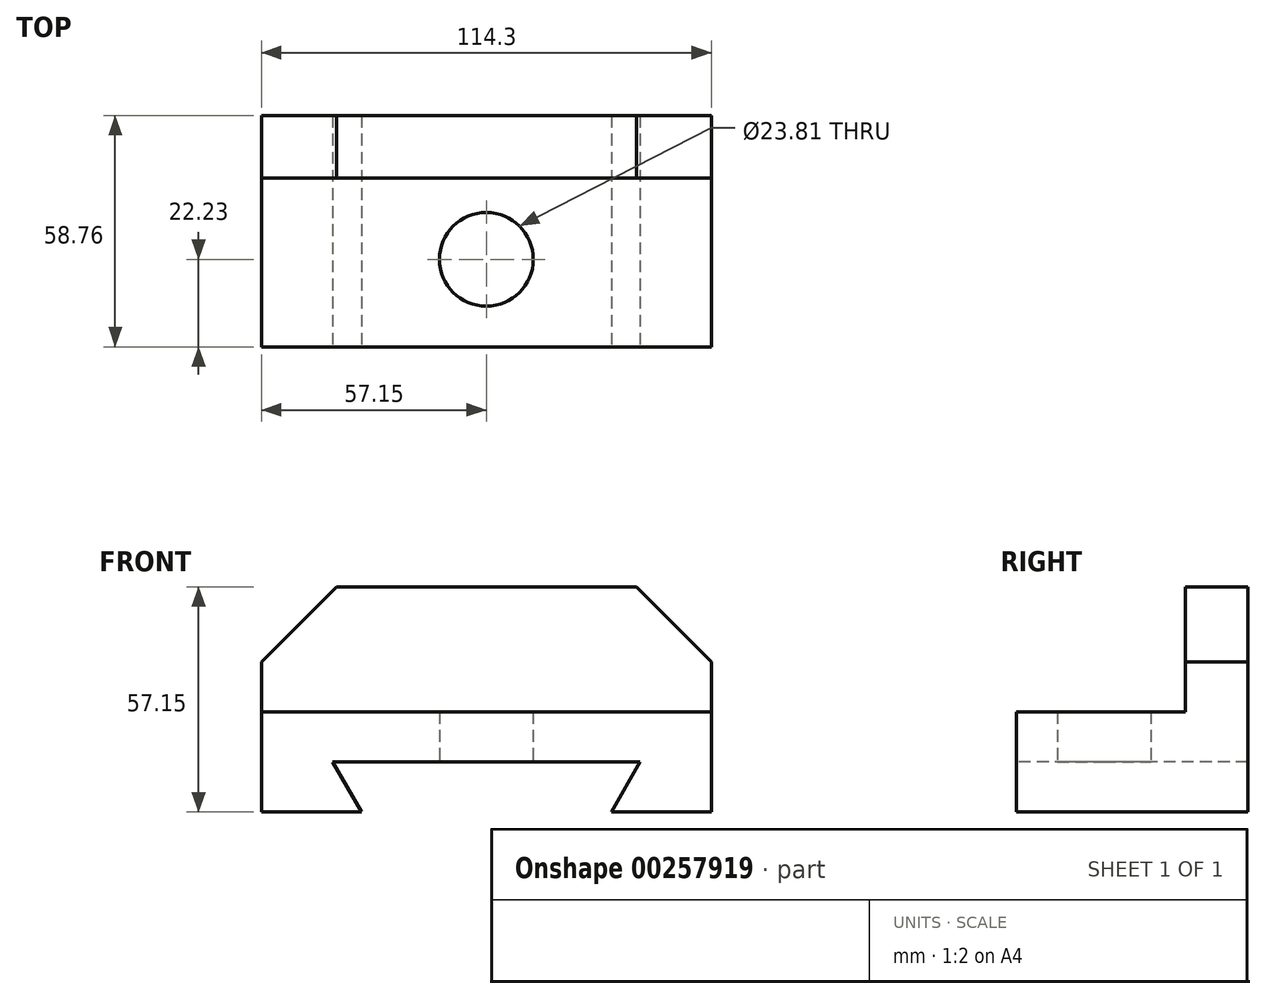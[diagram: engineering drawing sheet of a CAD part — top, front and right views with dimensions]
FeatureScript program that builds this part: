
annotation { "Feature Type Name" : "Feature", "Feature Type Description" : "" }
export const myFeature = defineFeature(function(context is Context, id is Id, definition is map)
    precondition{}
    {
        {
            var Q0;
            Q0=qCreatedBy(makeId("Top.planeOp"),FACE);
            var sketch = newSketch(context, id + "F0", { "sketchPlane" : qUnion([Q0])});
            skCircle(sketch, "E0", {"center": v(0, 0) * mm, "radius": 11.9 * mm});
            skLineSegment(sketch, "E1", {"start": v(0, 0) * mm, "end": v(0, -22.23) * mm});
            skLineSegment(sketch, "E2", {"start": v(0, -22.23) * mm, "end": v(-57.15, -22.23) * mm});
            skLineSegment(sketch, "E3.MirrorCS", {"start": v(0, -22.23) * mm, "end": v(57.15, -22.23) * mm});
            skLineSegment(sketch, "E4", {"start": v(0, 0) * mm, "end": v(-57.15, 0) * mm});
            skLineSegment(sketch, "E5", {"start": v(-57.15, 0) * mm, "end": v(-57.15, -22.23) * mm});
            skPoint(sketch, "E6.MirrorCS.end.orphan", {"position": v(57.15, 22.22) * mm});
            skPoint(sketch, "E6.MirrorCS.start.orphan", {"position": v(57.15, -22.23) * mm});
            skPoint(sketch, "E7.MirrorCS.end.orphan", {"position": v(0, 22.22) * mm});
            skLineSegment(sketch, "E8", {"start": v(-57.15, 0) * mm, "end": v(-57.15, 20.65) * mm});
            skLineSegment(sketch, "E9.MirrorCS", {"start": v(57.15, 0) * mm, "end": v(57.15, 20.65) * mm});
            skLineSegment(sketch, "E10.MirrorCS", {"start": v(0, 0) * mm, "end": v(57.15, 0) * mm});
            skLineSegment(sketch, "E11.MirrorCS", {"start": v(57.15, 0) * mm, "end": v(57.15, -22.23) * mm});
            skLineSegment(sketch, "E12", {"start": v(-57.15, 20.65) * mm, "end": v(57.15, 20.65) * mm});
            skLineSegment(sketch, "E13", {"start": v(-57.15, 20.65) * mm, "end": v(-57.15, 36.53) * mm});
            skLineSegment(sketch, "E14", {"start": v(-57.15, 36.53) * mm, "end": v(57.15, 36.53) * mm});
            skLineSegment(sketch, "E15", {"start": v(57.15, 20.65) * mm, "end": v(57.15, 36.53) * mm});
            skLineSegment(sketch, "E16", {"start": v(-57.15, 36.53) * mm, "end": v(-38.1, 36.53) * mm});
            skLineSegment(sketch, "E17", {"start": v(-38.1, 36.53) * mm, "end": v(-38.1, 20.65) * mm});
            skLineSegment(sketch, "E18.MirrorCS", {"start": v(38.1, 36.53) * mm, "end": v(38.1, 20.65) * mm});
            skLineSegment(sketch, "E19.MirrorCS", {"start": v(57.15, 36.53) * mm, "end": v(38.1, 36.53) * mm});
            skSolve(sketch);
        }
        {
            var Q0;
            {var subQ0=sQuery(id+"F0.wireOp",EDGE,"E13");Q0=makeQuery(id+"F0.imprint","IMPRINT",FACE,{"disambiguationData":[TD([[makeQuery(id+"F0.imprint","IMPRINT",EDGE,{"derivedFrom":subQ0}),-1.0]])]});}
            var Q1;
            Q1=makeQuery(id+"F0.imprint","IMPRINT",FACE,{"disambiguationData":[TD([[makeQuery(id+"F0.imprint","IMPRINT",EDGE,{"derivedFrom":sQuery(id+"F0.wireOp",EDGE,"E14")}),-1.0]])]});
            var Q2;
            {var subQ0=sQuery(id+"F0.wireOp",EDGE,"E15");Q2=makeQuery(id+"F0.imprint","IMPRINT",FACE,{"disambiguationData":[TD([[makeQuery(id+"F0.imprint","IMPRINT",EDGE,{"derivedFrom":subQ0}),1.0]])]});}
            extrude(context, id + "F1", {"entities" : qUnion([Q0, Q1, Q2]), "depth" : 57.15 * mm});
        }
        {
            var Q0;
            {var subQ1=sQuery(id+"F0.wireOp",EDGE,"E8");Q0=makeQuery(id+"F0.imprint","IMPRINT",FACE,{"disambiguationData":[TD([[makeQuery(id+"F0.imprint","IMPRINT",EDGE,{"derivedFrom":subQ1}),-1.0]])]});}
            var Q1;
            {var subQ4=sQuery(id+"F0.wireOp",EDGE,"E2");Q1=makeQuery(id+"F0.imprint","IMPRINT",FACE,{"disambiguationData":[TD([[makeQuery(id+"F0.imprint","IMPRINT",EDGE,{"derivedFrom":subQ4}),-1.0]])]});}
            var Q2;
            {var subQ0=sQuery(id+"F0.wireOp",EDGE,"E11.MirrorCS");Q2=makeQuery(id+"F0.imprint","IMPRINT",FACE,{"disambiguationData":[TD([[makeQuery(id+"F0.imprint","IMPRINT",EDGE,{"derivedFrom":subQ0}),-1.0]])]});}
            extrude(context, id + "F2", {"entities" : qUnion([Q0, Q1, Q2]), "operationType" : NewBodyOperationType.ADD, "depth" : 25.4 * mm});
        }
        {
            var Q0;
            Q0=makeQuery(id+"F1.opExtrude","SWEPT_FACE",FACE,{"disambiguationData":[OSD([sQuery(id+"F0.wireOp",EDGE,"E12")])]});
            var sketch = newSketch(context, id + "F3", { "sketchPlane" : qUnion([Q0])});
            skLineSegment(sketch, "E20", {"start": v(-57.15, 57.15) * mm, "end": v(-38.1, 57.15) * mm});
            skLineSegment(sketch, "E21", {"start": v(-57.15, 57.15) * mm, "end": v(-57.15, 38.1) * mm});
            skLineSegment(sketch, "E22", {"start": v(-38.1, 57.15) * mm, "end": v(-57.15, 38.1) * mm});
            skLineSegment(sketch, "E23.MirrorCS", {"start": v(57.15, 57.15) * mm, "end": v(38.1, 57.15) * mm});
            skLineSegment(sketch, "E24.MirrorCS", {"start": v(57.15, 57.15) * mm, "end": v(57.15, 38.1) * mm});
            skLineSegment(sketch, "E25.MirrorCS", {"start": v(38.1, 57.15) * mm, "end": v(57.15, 38.1) * mm});
            skSolve(sketch);
        }
        {
            var Q0;
            Q0=makeQuery(id+"F3.imprint","IMPRINT",FACE,{"disambiguationData":[TD([[makeQuery(id+"F3.imprint","IMPRINT",EDGE,{"derivedFrom":sQuery(id+"F3.wireOp",EDGE,"E20")}),-1.0]])]});
            var Q1;
            Q1=makeQuery(id+"F3.imprint","IMPRINT",FACE,{"disambiguationData":[TD([[makeQuery(id+"F3.imprint","IMPRINT",EDGE,{"derivedFrom":sQuery(id+"F3.wireOp",EDGE,"E23.MirrorCS")}),-1.0]])]});
            extrude(context, id + "F4", {"entities" : qUnion([Q0, Q1]), "operationType" : NewBodyOperationType.REMOVE, "oppositeDirection" : true, "depth" : 15.88 * mm});
        }
        {
            var Q0;
            Q0=makeQuery(id+"F2.opExtrude","SWEPT_FACE",FACE,{"disambiguationData":[OSD([sQuery(id+"F0.wireOp",EDGE,"E2"),sQuery(id+"F0.wireOp",EDGE,"E3.MirrorCS")])]});
            var sketch = newSketch(context, id + "F5", { "sketchPlane" : qUnion([Q0])});
            skLineSegment(sketch, "E26", {"start": v(-57.15, 25.4) * mm, "end": v(-57.15, 0) * mm});
            skLineSegment(sketch, "E27", {"start": v(-57.15, 0) * mm, "end": v(-31.75, 0) * mm});
            skLineSegment(sketch, "E28", {"start": v(-57.15, 25.4) * mm, "end": v(57.15, 25.4) * mm});
            skLineSegment(sketch, "E29", {"start": v(-31.75, 0) * mm, "end": v(-38.55, 11.78) * mm});
            skLineSegment(sketch, "E30", {"start": v(0, 0) * mm, "end": v(0, 12.7) * mm});
            skPoint(sketch, "E30.endSnap0", {"position": v(0, 0) * mm});
            skLineSegment(sketch, "E31", {"start": v(0, 12.7) * mm, "end": v(-39.08, 12.7) * mm});
            skLineSegment(sketch, "E32", {"start": v(-38.55, 11.78) * mm, "end": v(-39.08, 12.7) * mm});
            skPoint(sketch, "E33.orphan", {"position": v(-43.62, 12.7) * mm});
            skPoint(sketch, "E34.orphan", {"position": v(-43.62, 20.56) * mm});
            skLineSegment(sketch, "E35.MirrorCS", {"start": v(31.75, 0) * mm, "end": v(38.55, 11.78) * mm});
            skLineSegment(sketch, "E36.MirrorCS", {"start": v(57.15, 0) * mm, "end": v(31.75, 0) * mm});
            skLineSegment(sketch, "E37.MirrorCS", {"start": v(0, 12.7) * mm, "end": v(39.08, 12.7) * mm});
            skLineSegment(sketch, "E38", {"start": v(57.15, 25.4) * mm, "end": v(57.15, 0) * mm});
            skLineSegment(sketch, "E39", {"start": v(-31.75, 0) * mm, "end": v(0, 0) * mm});
            skLineSegment(sketch, "E40", {"start": v(31.75, 0) * mm, "end": v(0, 0) * mm});
            skLineSegment(sketch, "E41", {"start": v(39.08, 12.7) * mm, "end": v(31.75, 0) * mm});
            skSolve(sketch);
        }
        {
            var Q0;
            Q0=makeQuery(id+"F5.imprint","IMPRINT",FACE,{"disambiguationData":[TD([[makeQuery(id+"F5.imprint","IMPRINT",EDGE,{"derivedFrom":sQuery(id+"F5.wireOp",EDGE,"E29")}),-1.0]])]});
            var Q1;
            Q1=makeQuery(id+"F5.imprint","IMPRINT",FACE,{"disambiguationData":[TD([[makeQuery(id+"F5.imprint","IMPRINT",EDGE,{"derivedFrom":sQuery(id+"F5.wireOp",EDGE,"E30")}),-1.0]])]});
            extrude(context, id + "F6", {"entities" : qUnion([Q0, Q1]), "operationType" : NewBodyOperationType.REMOVE, "oppositeDirection" : true, "depth" : 58.75 * mm});
        }
    });
